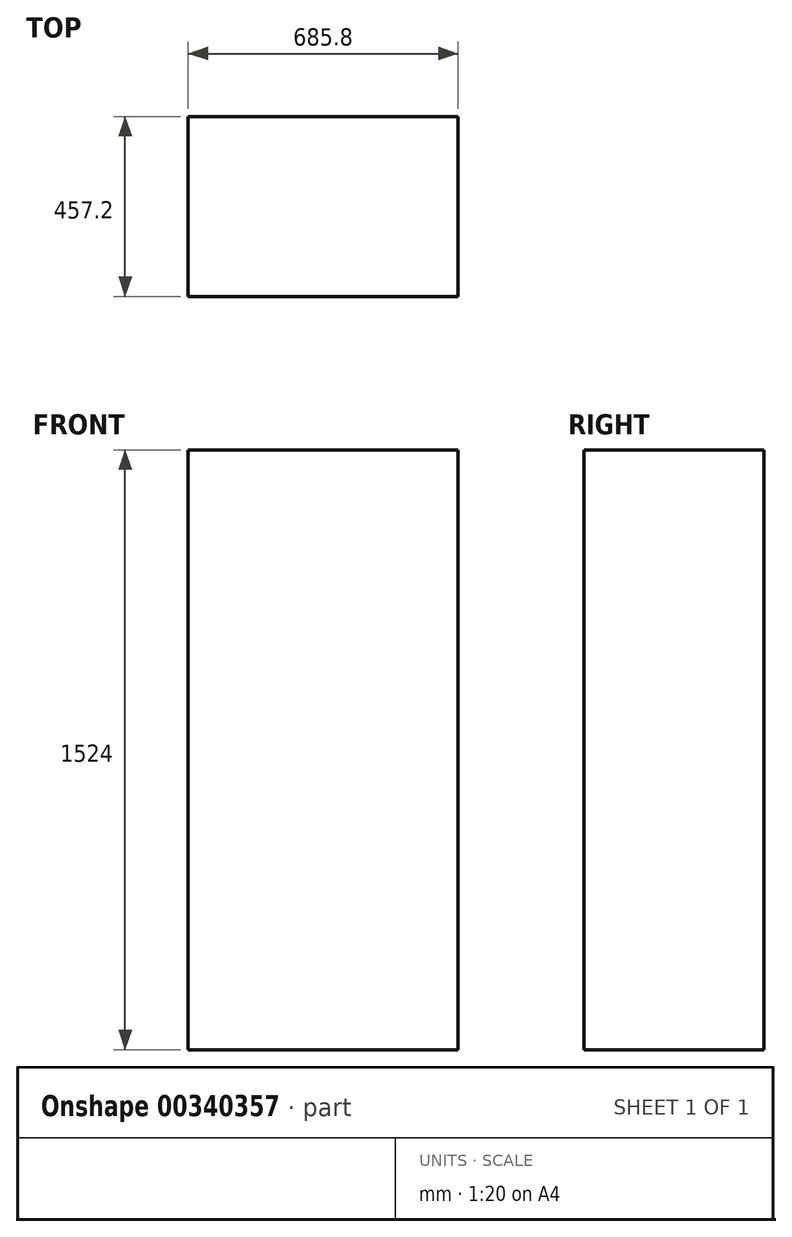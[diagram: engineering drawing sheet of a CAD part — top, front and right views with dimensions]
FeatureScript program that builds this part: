
annotation { "Feature Type Name" : "Feature", "Feature Type Description" : "" }
export const myFeature = defineFeature(function(context is Context, id is Id, definition is map)
    precondition{}
    {
        {
            var Q0;
            Q0=qCreatedBy(makeId("Front.planeOp"),FACE);
            var sketch = newSketch(context, id + "F0", { "sketchPlane" : qUnion([Q0])});
            skLineSegment(sketch, "E0.bottom", {"start": v(-342.9, 762) * mm, "end": v(342.9, 762) * mm});
            skLineSegment(sketch, "E0.top", {"start": v(-342.9, -762) * mm, "end": v(342.9, -762) * mm});
            skLineSegment(sketch, "E0.left", {"start": v(-342.9, 762) * mm, "end": v(-342.9, -762) * mm});
            skLineSegment(sketch, "E0.right", {"start": v(342.9, 762) * mm, "end": v(342.9, -762) * mm});
            skPoint(sketch, "E0.middle", {"position": v(0, 0) * mm});
            skSolve(sketch);
        }
        {
            var Q0;
            Q0 = qSketchRegion(id + "F0", true);
            extrude(context, id + "F1", {"entities" : qUnion([Q0]), "depth" : 457.2 * mm});
        }
    });
